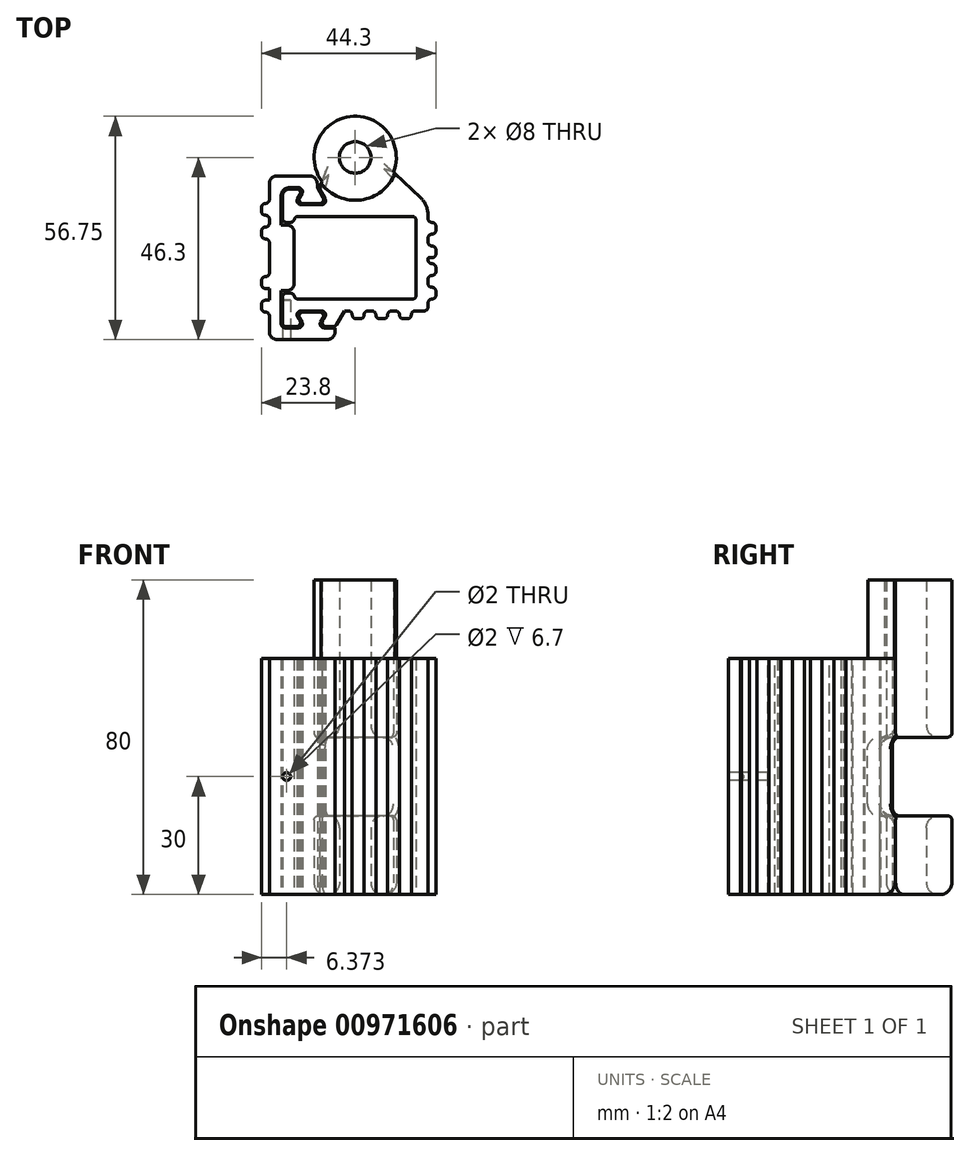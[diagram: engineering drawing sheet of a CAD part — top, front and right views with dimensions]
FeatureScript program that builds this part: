
annotation { "Feature Type Name" : "Feature", "Feature Type Description" : "" }
export const myFeature = defineFeature(function(context is Context, id is Id, definition is map)
    precondition{}
    {
        {
            var Q0;
            Q0=qCreatedBy(makeId("Top.planeOp"),FACE);
            var sketch = newSketch(context, id + "F0", { "sketchPlane" : qUnion([Q0])});
            skLineSegment(sketch, "E0.bottom", {"start": v(15.5, -10.5) * mm, "end": v(-15.5, -10.5) * mm, "construction": true});
            skLineSegment(sketch, "E0.top", {"start": v(15.5, 10.5) * mm, "end": v(-15.5, 10.5) * mm, "construction": true});
            skLineSegment(sketch, "E0.left", {"start": v(15.5, -10.5) * mm, "end": v(15.5, 10.5) * mm, "construction": true});
            skLineSegment(sketch, "E0.right", {"start": v(-15.5, -10.5) * mm, "end": v(-15.5, 10.25) * mm, "construction": true});
            skPoint(sketch, "E0.middle", {"position": v(0, 0) * mm});
            skLineSegment(sketch, "E1", {"start": v(-15.5, 0) * mm, "end": v(-15.5, -10.5) * mm});
            skLineSegment(sketch, "E2", {"start": v(15.5, -10.5) * mm, "end": v(15.5, 0) * mm});
            skLineSegment(sketch, "E3", {"start": v(15.5, 0) * mm, "end": v(18.5, 0) * mm});
            skLineSegment(sketch, "E4", {"start": v(-1.76, -13.5) * mm, "end": v(-2.76, -13.5) * mm});
            skLineSegment(sketch, "E5", {"start": v(-15.5, -10.5) * mm, "end": v(-15.5, -9) * mm});
            skLineSegment(sketch, "E6", {"start": v(-15.5, -9) * mm, "end": v(-17.5, -9) * mm});
            skLineSegment(sketch, "E7", {"start": v(-18.5, -10) * mm, "end": v(-18.5, -13.5) * mm});
            skLineSegment(sketch, "E8", {"start": v(-14.63, -15) * mm, "end": v(-14.06, -16) * mm});
            skLineSegment(sketch, "E9", {"start": v(-8.24, -16) * mm, "end": v(-7.67, -15) * mm});
            skLineSegment(sketch, "E10", {"start": v(-8.53, -13.5) * mm, "end": v(-13.77, -13.5) * mm});
            skLineSegment(sketch, "E11", {"start": v(-2.76, -13.5) * mm, "end": v(-5.07, -17.5) * mm});
            skLineSegment(sketch, "E12", {"start": v(-5.07, -17.5) * mm, "end": v(-7.38, -17.5) * mm});
            skLineSegment(sketch, "E13", {"start": v(-14.92, -17.5) * mm, "end": v(-17.5, -17.5) * mm});
            skLineSegment(sketch, "E14", {"start": v(-18.5, -16.5) * mm, "end": v(-18.5, -13.5) * mm});
            skLineSegment(sketch, "E15", {"start": v(-15.5, -13.5) * mm, "end": v(-15.5, -13.5) * mm});
            skLineSegment(sketch, "E16", {"start": v(-6.8, -13.5) * mm, "end": v(-15.5, -13.5) * mm});
            skLineSegment(sketch, "E17", {"start": v(-18.44, -13.5) * mm, "end": v(-18.5, -13.5) * mm});
            skLineSegment(sketch, "E18.0", {"start": v(-18.8, -9) * mm, "end": v(-18.8, -13.5) * mm});
            skLineSegment(sketch, "E18.1", {"start": v(-18.8, -16.8) * mm, "end": v(-18.8, -13.5) * mm});
            skLineSegment(sketch, "E18.2", {"start": v(-14.4, -17.8) * mm, "end": v(-17.8, -17.8) * mm});
            skLineSegment(sketch, "E18.3", {"start": v(-5.13, -17.8) * mm, "end": v(-7.9, -17.8) * mm});
            skLineSegment(sketch, "E18.4", {"start": v(-8.76, -16.3) * mm, "end": v(-8.19, -15.3) * mm});
            skLineSegment(sketch, "E18.5", {"start": v(-9.05, -13.8) * mm, "end": v(-13.25, -13.8) * mm});
            skLineSegment(sketch, "E18.6", {"start": v(-14.11, -15.3) * mm, "end": v(-13.54, -16.3) * mm});
            skLineSegment(sketch, "E19", {"start": v(-5.13, -17.8) * mm, "end": v(-5.13, -18.8) * mm});
            skLineSegment(sketch, "E20", {"start": v(-7.13, -20.8) * mm, "end": v(-19.8, -20.8) * mm});
            skLineSegment(sketch, "E21", {"start": v(-21.8, -18.8) * mm, "end": v(-21.8, -9) * mm});
            skLineSegment(sketch, "E22", {"start": v(-15.5, -10.5) * mm, "end": v(15.5, -10.5) * mm});
            skLineSegment(sketch, "E23.MirrorCS", {"start": v(-15.5, 9) * mm, "end": v(-18.5, 9) * mm});
            skLineSegment(sketch, "E24.MirrorCS", {"start": v(-18.44, 13.5) * mm, "end": v(-18.5, 13.5) * mm});
            skLineSegment(sketch, "E25.MirrorCS", {"start": v(-8.53, 13.5) * mm, "end": v(-13.77, 13.5) * mm});
            skLineSegment(sketch, "E26.MirrorCS", {"start": v(-14.63, 15) * mm, "end": v(-14.06, 16) * mm});
            skLineSegment(sketch, "E27.MirrorCS", {"start": v(-6.8, 13.5) * mm, "end": v(-15.5, 13.5) * mm});
            skLineSegment(sketch, "E28.MirrorCS", {"start": v(-9.1, 17.5) * mm, "end": v(-7.67, 15) * mm});
            skLineSegment(sketch, "E29.MirrorCS", {"start": v(-9.63, 17.8) * mm, "end": v(-8.19, 15.3) * mm});
            skLineSegment(sketch, "E30.MirrorCS", {"start": v(-15.5, 13.5) * mm, "end": v(-15.5, 13.5) * mm});
            skLineSegment(sketch, "E31.MirrorCS", {"start": v(-14.4, 17.8) * mm, "end": v(-16.8, 17.8) * mm});
            skLineSegment(sketch, "E32.MirrorCS", {"start": v(-9.05, 13.8) * mm, "end": v(-13.25, 13.8) * mm});
            skLineSegment(sketch, "E33.MirrorCS", {"start": v(-14.11, 15.3) * mm, "end": v(-13.54, 16.3) * mm});
            skLineSegment(sketch, "E34.MirrorCS", {"start": v(-14.92, 17.5) * mm, "end": v(-16.5, 17.5) * mm});
            skLineSegment(sketch, "E35.MirrorCS", {"start": v(-18.5, 15.5) * mm, "end": v(-18.5, 13.5) * mm});
            skLineSegment(sketch, "E36.MirrorCS", {"start": v(-18.8, 15.8) * mm, "end": v(-18.8, 13.5) * mm});
            skLineSegment(sketch, "E37.MirrorCS", {"start": v(-21.8, 18.8) * mm, "end": v(-21.8, 9) * mm});
            skLineSegment(sketch, "E38.MirrorCS", {"start": v(-15.5, 9) * mm, "end": v(-17.5, 9) * mm});
            skLineSegment(sketch, "E39.MirrorCS", {"start": v(-18.5, 10) * mm, "end": v(-18.5, 13.5) * mm});
            skLineSegment(sketch, "E40.MirrorCS", {"start": v(-18.8, 9) * mm, "end": v(-18.8, 13.5) * mm});
            skLineSegment(sketch, "E41.MirrorCS", {"start": v(-15.5, 6.37) * mm, "end": v(-15.5, -6.38) * mm, "construction": true});
            skLineSegment(sketch, "E42.MirrorCS", {"start": v(15.5, 10.5) * mm, "end": v(-15.25, 10.5) * mm, "construction": true});
            skLineSegment(sketch, "E43", {"start": v(-15.5, 10.5) * mm, "end": v(15.5, 10.5) * mm});
            skLineSegment(sketch, "E44", {"start": v(15.5, 0) * mm, "end": v(15.5, 10.5) * mm});
            skLineSegment(sketch, "E45", {"start": v(-15.5, 10.5) * mm, "end": v(-15.5, 9) * mm});
            skLineSegment(sketch, "E46", {"start": v(-21.8, -9) * mm, "end": v(-21.8, 9) * mm});
            skLineSegment(sketch, "E47", {"start": v(0, 10.5) * mm, "end": v(0, 25.5) * mm, "construction": true});
            skCircle(sketch, "E48", {"center": v(0, 25.5) * mm, "radius": 4 * mm});
            skLineSegment(sketch, "E49", {"start": v(-9.63, 17.8) * mm, "end": v(-9.63, 18.8) * mm});
            skLineSegment(sketch, "E50", {"start": v(-11.63, 20.8) * mm, "end": v(-19.8, 20.8) * mm});
            skArc(sketch, "E51", {"start": v(9.72, 21.68) * mm, "mid": v(-1.34, 35.86) * mm, "end": v(-8.44, 19.34) * mm});
            skLineSegment(sketch, "E52", {"start": v(-8.44, 19.34) * mm, "end": v(-9.1, 17.5) * mm});
            skLineSegment(sketch, "E53", {"start": v(9.72, 21.68) * mm, "end": v(18.5, 13.5) * mm});
            skLineSegment(sketch, "E54", {"start": v(19.5, -10.5) * mm, "end": v(19.5, -10.5) * mm});
            skLineSegment(sketch, "E55", {"start": v(20.5, -9.5) * mm, "end": v(20.5, -8.5) * mm});
            skLineSegment(sketch, "E56", {"start": v(19.5, -7.5) * mm, "end": v(19.5, -7.5) * mm});
            skLineSegment(sketch, "E57", {"start": v(18.5, -6.5) * mm, "end": v(18.5, -5.5) * mm});
            skLineSegment(sketch, "E58", {"start": v(19.5, -4.5) * mm, "end": v(19.5, -4.5) * mm});
            skLineSegment(sketch, "E59", {"start": v(20.5, -3.5) * mm, "end": v(20.5, -2.5) * mm});
            skLineSegment(sketch, "E60", {"start": v(19.5, -1.5) * mm, "end": v(19.5, -1.5) * mm});
            skLineSegment(sketch, "E61", {"start": v(18.5, -0.5) * mm, "end": v(18.5, -0.25) * mm});
            skLineSegment(sketch, "E62", {"start": v(20.5, 1) * mm, "end": v(20.5, 2) * mm});
            skLineSegment(sketch, "E63", {"start": v(19.5, 3) * mm, "end": v(19.5, 3) * mm});
            skLineSegment(sketch, "E64", {"start": v(18.5, 4) * mm, "end": v(18.5, 5) * mm});
            skLineSegment(sketch, "E65", {"start": v(19.5, 6) * mm, "end": v(19.5, 6) * mm});
            skLineSegment(sketch, "E66", {"start": v(20.5, 7) * mm, "end": v(20.5, 8) * mm});
            skLineSegment(sketch, "E67", {"start": v(19.5, 9) * mm, "end": v(19.5, 9) * mm});
            skLineSegment(sketch, "E68", {"start": v(18.5, 10) * mm, "end": v(18.5, 11.5) * mm});
            skLineSegment(sketch, "E69", {"start": v(19.5, 0) * mm, "end": v(18.75, 0) * mm});
            skLineSegment(sketch, "E70", {"start": v(18.5, 13.5) * mm, "end": v(18.5, 11.82) * mm});
            skLineSegment(sketch, "E71", {"start": v(18.5, -11.5) * mm, "end": v(18.5, -12.5) * mm});
            skLineSegment(sketch, "E72", {"start": v(18.5, 11.82) * mm, "end": v(18.5, 11.5) * mm});
            skLineSegment(sketch, "E73", {"start": v(-0.76, -14.5) * mm, "end": v(-0.76, -14.5) * mm});
            skLineSegment(sketch, "E74", {"start": v(0.24, -15.5) * mm, "end": v(1.24, -15.5) * mm});
            skLineSegment(sketch, "E75", {"start": v(2.24, -14.5) * mm, "end": v(2.24, -14.5) * mm});
            skLineSegment(sketch, "E76", {"start": v(3.24, -13.5) * mm, "end": v(4.24, -13.5) * mm});
            skLineSegment(sketch, "E77", {"start": v(5.24, -14.5) * mm, "end": v(5.24, -14.5) * mm});
            skLineSegment(sketch, "E78", {"start": v(6.24, -15.5) * mm, "end": v(7.24, -15.5) * mm});
            skLineSegment(sketch, "E79", {"start": v(8.24, -14.5) * mm, "end": v(8.24, -14.5) * mm});
            skLineSegment(sketch, "E80", {"start": v(9.24, -13.5) * mm, "end": v(10.24, -13.5) * mm});
            skLineSegment(sketch, "E81", {"start": v(11.24, -14.5) * mm, "end": v(11.24, -14.5) * mm});
            skLineSegment(sketch, "E82", {"start": v(12.24, -15.5) * mm, "end": v(13.24, -15.5) * mm});
            skLineSegment(sketch, "E83", {"start": v(14.24, -14.5) * mm, "end": v(14.24, -14.5) * mm});
            skPoint(sketch, "E84.visualSharp", {"position": v(-0.76, -15.5) * mm});
            skArc(sketch, "E84.filletArc", {"start": v(-0.76, -14.5) * mm, "mid": v(-0.47, -15.2) * mm, "end": v(0.24, -15.5) * mm});
            skPoint(sketch, "E85.newPointA", {"position": v(18.5, -13.5) * mm});
            skPoint(sketch, "E85.newPointB", {"position": v(-0.76, -13.5) * mm});
            skArc(sketch, "E85.filletArc", {"start": v(-0.76, -14.5) * mm, "mid": v(-1.05, -13.8) * mm, "end": v(-1.76, -13.5) * mm});
            skPoint(sketch, "E86.visualSharp", {"position": v(2.24, -15.5) * mm});
            skArc(sketch, "E86.filletArc", {"start": v(1.24, -15.5) * mm, "mid": v(1.95, -15.2) * mm, "end": v(2.24, -14.5) * mm});
            skPoint(sketch, "E87.visualSharp", {"position": v(2.24, -13.5) * mm});
            skArc(sketch, "E87.filletArc", {"start": v(3.24, -13.5) * mm, "mid": v(2.53, -13.8) * mm, "end": v(2.24, -14.5) * mm});
            skPoint(sketch, "E88.visualSharp", {"position": v(5.24, -13.5) * mm});
            skArc(sketch, "E88.filletArc", {"start": v(5.24, -14.5) * mm, "mid": v(4.95, -13.8) * mm, "end": v(4.24, -13.5) * mm});
            skPoint(sketch, "E89.visualSharp", {"position": v(5.24, -15.5) * mm});
            skArc(sketch, "E89.filletArc", {"start": v(5.24, -14.5) * mm, "mid": v(5.53, -15.2) * mm, "end": v(6.24, -15.5) * mm});
            skPoint(sketch, "E90.visualSharp", {"position": v(8.24, -15.5) * mm});
            skArc(sketch, "E90.filletArc", {"start": v(7.24, -15.5) * mm, "mid": v(7.95, -15.2) * mm, "end": v(8.24, -14.5) * mm});
            skPoint(sketch, "E91.visualSharp", {"position": v(8.24, -13.5) * mm});
            skArc(sketch, "E91.filletArc", {"start": v(9.24, -13.5) * mm, "mid": v(8.53, -13.8) * mm, "end": v(8.24, -14.5) * mm});
            skPoint(sketch, "E92.visualSharp", {"position": v(11.24, -13.5) * mm});
            skArc(sketch, "E92.filletArc", {"start": v(11.24, -14.5) * mm, "mid": v(10.95, -13.8) * mm, "end": v(10.24, -13.5) * mm});
            skPoint(sketch, "E93.visualSharp", {"position": v(11.24, -15.5) * mm});
            skArc(sketch, "E93.filletArc", {"start": v(11.24, -14.5) * mm, "mid": v(11.53, -15.2) * mm, "end": v(12.24, -15.5) * mm});
            skPoint(sketch, "E94.visualSharp", {"position": v(14.24, -15.5) * mm});
            skArc(sketch, "E94.filletArc", {"start": v(13.24, -15.5) * mm, "mid": v(13.95, -15.2) * mm, "end": v(14.24, -14.5) * mm});
            skLineSegment(sketch, "E95", {"start": v(15.24, -13.5) * mm, "end": v(17.5, -13.5) * mm});
            skPoint(sketch, "E96.visualSharp", {"position": v(14.24, -13.5) * mm});
            skArc(sketch, "E96.filletArc", {"start": v(15.24, -13.5) * mm, "mid": v(14.53, -13.8) * mm, "end": v(14.24, -14.5) * mm});
            skArc(sketch, "E97.filletArc", {"start": v(17.5, -13.5) * mm, "mid": v(18.2, -13.2) * mm, "end": v(18.5, -12.5) * mm});
            skPoint(sketch, "E98.visualSharp", {"position": v(18.5, -10.5) * mm});
            skArc(sketch, "E98.filletArc", {"start": v(19.5, -10.5) * mm, "mid": v(18.8, -10.8) * mm, "end": v(18.5, -11.5) * mm});
            skPoint(sketch, "E99.visualSharp", {"position": v(20.5, -10.5) * mm});
            skArc(sketch, "E99.filletArc", {"start": v(19.5, -10.5) * mm, "mid": v(20.2, -10.2) * mm, "end": v(20.5, -9.5) * mm});
            skPoint(sketch, "E100.visualSharp", {"position": v(20.5, -7.5) * mm});
            skArc(sketch, "E100.filletArc", {"start": v(20.5, -8.5) * mm, "mid": v(20.2, -7.8) * mm, "end": v(19.5, -7.5) * mm});
            skPoint(sketch, "E101.visualSharp", {"position": v(18.5, -7.5) * mm});
            skArc(sketch, "E101.filletArc", {"start": v(18.5, -6.5) * mm, "mid": v(18.8, -7.2) * mm, "end": v(19.5, -7.5) * mm});
            skPoint(sketch, "E102.visualSharp", {"position": v(18.5, -4.5) * mm});
            skArc(sketch, "E102.filletArc", {"start": v(19.5, -4.5) * mm, "mid": v(18.8, -4.8) * mm, "end": v(18.5, -5.5) * mm});
            skPoint(sketch, "E103.visualSharp", {"position": v(20.5, -4.5) * mm});
            skArc(sketch, "E103.filletArc", {"start": v(19.5, -4.5) * mm, "mid": v(20.2, -4.2) * mm, "end": v(20.5, -3.5) * mm});
            skPoint(sketch, "E104.visualSharp", {"position": v(20.5, -1.5) * mm});
            skArc(sketch, "E104.filletArc", {"start": v(20.5, -2.5) * mm, "mid": v(20.2, -1.8) * mm, "end": v(19.5, -1.5) * mm});
            skPoint(sketch, "E105.visualSharp", {"position": v(18.5, -1.5) * mm});
            skArc(sketch, "E105.filletArc", {"start": v(18.5, -0.5) * mm, "mid": v(18.8, -1.2) * mm, "end": v(19.5, -1.5) * mm});
            skPoint(sketch, "E106.visualSharp", {"position": v(18.5, 0) * mm});
            skArc(sketch, "E106.filletArc", {"start": v(18.75, 0) * mm, "mid": v(18.57, -0.07) * mm, "end": v(18.5, -0.25) * mm});
            skPoint(sketch, "E107.visualSharp", {"position": v(20.5, 0) * mm});
            skArc(sketch, "E107.filletArc", {"start": v(19.5, 0) * mm, "mid": v(20.2, 0.3) * mm, "end": v(20.5, 1) * mm});
            skPoint(sketch, "E108.visualSharp", {"position": v(20.5, 3) * mm});
            skArc(sketch, "E108.filletArc", {"start": v(20.5, 2) * mm, "mid": v(20.2, 2.7) * mm, "end": v(19.5, 3) * mm});
            skPoint(sketch, "E109.visualSharp", {"position": v(18.5, 3) * mm});
            skArc(sketch, "E109.filletArc", {"start": v(18.5, 4) * mm, "mid": v(18.8, 3.3) * mm, "end": v(19.5, 3) * mm});
            skPoint(sketch, "E110.visualSharp", {"position": v(18.5, 6) * mm});
            skArc(sketch, "E110.filletArc", {"start": v(19.5, 6) * mm, "mid": v(18.8, 5.7) * mm, "end": v(18.5, 5) * mm});
            skPoint(sketch, "E111.visualSharp", {"position": v(20.5, 6) * mm});
            skArc(sketch, "E111.filletArc", {"start": v(19.5, 6) * mm, "mid": v(20.2, 6.3) * mm, "end": v(20.5, 7) * mm});
            skPoint(sketch, "E112.visualSharp", {"position": v(20.5, 9) * mm});
            skArc(sketch, "E112.filletArc", {"start": v(20.5, 8) * mm, "mid": v(20.2, 8.7) * mm, "end": v(19.5, 9) * mm});
            skPoint(sketch, "E113.visualSharp", {"position": v(18.5, 9) * mm});
            skArc(sketch, "E113.filletArc", {"start": v(18.5, 10) * mm, "mid": v(18.8, 9.3) * mm, "end": v(19.5, 9) * mm});
            skPoint(sketch, "E114.visualSharp", {"position": v(-15.5, 10.5) * mm});
            skArc(sketch, "E114.filletArc", {"start": v(-15.25, 10.5) * mm, "mid": v(-15.43, 10.43) * mm, "end": v(-15.5, 10.25) * mm, "construction": true});
            skPoint(sketch, "E115.visualSharp", {"position": v(-5.13, -20.8) * mm});
            skArc(sketch, "E115.filletArc", {"start": v(-7.13, -20.8) * mm, "mid": v(-5.71, -20.21) * mm, "end": v(-5.13, -18.8) * mm});
            skPoint(sketch, "E116.visualSharp", {"position": v(-9.63, 20.8) * mm});
            skArc(sketch, "E116.filletArc", {"start": v(-9.63, 18.8) * mm, "mid": v(-10.21, 20.21) * mm, "end": v(-11.63, 20.8) * mm});
            skPoint(sketch, "E117.visualSharp", {"position": v(-21.8, 20.8) * mm});
            skArc(sketch, "E117.filletArc", {"start": v(-19.8, 20.8) * mm, "mid": v(-21.21, 20.21) * mm, "end": v(-21.8, 18.8) * mm});
            skPoint(sketch, "E118.visualSharp", {"position": v(-18.5, 17.5) * mm});
            skArc(sketch, "E118.filletArc", {"start": v(-16.5, 17.5) * mm, "mid": v(-17.91, 16.91) * mm, "end": v(-18.5, 15.5) * mm});
            skPoint(sketch, "E119.visualSharp", {"position": v(-18.8, 17.8) * mm});
            skArc(sketch, "E119.filletArc", {"start": v(-16.8, 17.8) * mm, "mid": v(-18.21, 17.21) * mm, "end": v(-18.8, 15.8) * mm});
            skPoint(sketch, "E120.visualSharp", {"position": v(-14.98, 13.8) * mm});
            skArc(sketch, "E120.filletArc", {"start": v(-14.11, 15.3) * mm, "mid": v(-14.11, 14.3) * mm, "end": v(-13.25, 13.8) * mm});
            skPoint(sketch, "E121.visualSharp", {"position": v(-15.5, 13.5) * mm});
            skArc(sketch, "E121.filletArc", {"start": v(-14.63, 15) * mm, "mid": v(-14.63, 14) * mm, "end": v(-13.77, 13.5) * mm});
            skPoint(sketch, "E122.visualSharp", {"position": v(-13.2, 17.5) * mm});
            skArc(sketch, "E122.filletArc", {"start": v(-14.06, 16) * mm, "mid": v(-14.06, 17) * mm, "end": v(-14.92, 17.5) * mm});
            skPoint(sketch, "E123.visualSharp", {"position": v(-12.67, 17.8) * mm});
            skArc(sketch, "E123.filletArc", {"start": v(-13.54, 16.3) * mm, "mid": v(-13.54, 17.3) * mm, "end": v(-14.4, 17.8) * mm});
            skPoint(sketch, "E124.visualSharp", {"position": v(-7.32, 13.8) * mm});
            skArc(sketch, "E124.filletArc", {"start": v(-9.05, 13.8) * mm, "mid": v(-8.19, 14.3) * mm, "end": v(-8.19, 15.3) * mm});
            skPoint(sketch, "E125.visualSharp", {"position": v(-6.8, 13.5) * mm});
            skArc(sketch, "E125.filletArc", {"start": v(-8.53, 13.5) * mm, "mid": v(-7.67, 14) * mm, "end": v(-7.67, 15) * mm});
            skPoint(sketch, "E126.visualSharp", {"position": v(-18.5, -17.5) * mm});
            skArc(sketch, "E126.filletArc", {"start": v(-18.5, -16.5) * mm, "mid": v(-18.2, -17.2) * mm, "end": v(-17.5, -17.5) * mm});
            skPoint(sketch, "E127.visualSharp", {"position": v(-18.8, -17.8) * mm});
            skArc(sketch, "E127.filletArc", {"start": v(-18.8, -16.8) * mm, "mid": v(-18.5, -17.5) * mm, "end": v(-17.8, -17.8) * mm});
            skPoint(sketch, "E128.visualSharp", {"position": v(-12.67, -17.8) * mm});
            skArc(sketch, "E128.filletArc", {"start": v(-14.4, -17.8) * mm, "mid": v(-13.54, -17.3) * mm, "end": v(-13.54, -16.3) * mm});
            skPoint(sketch, "E129.visualSharp", {"position": v(-13.2, -17.5) * mm});
            skArc(sketch, "E129.filletArc", {"start": v(-14.92, -17.5) * mm, "mid": v(-14.06, -17) * mm, "end": v(-14.06, -16) * mm});
            skPoint(sketch, "E130.visualSharp", {"position": v(-15.5, -13.5) * mm});
            skArc(sketch, "E130.filletArc", {"start": v(-13.77, -13.5) * mm, "mid": v(-14.63, -14) * mm, "end": v(-14.63, -15) * mm});
            skPoint(sketch, "E131.visualSharp", {"position": v(-14.98, -13.8) * mm});
            skArc(sketch, "E131.filletArc", {"start": v(-13.25, -13.8) * mm, "mid": v(-14.11, -14.3) * mm, "end": v(-14.11, -15.3) * mm});
            skPoint(sketch, "E132.visualSharp", {"position": v(-7.32, -13.8) * mm});
            skArc(sketch, "E132.filletArc", {"start": v(-8.19, -15.3) * mm, "mid": v(-8.19, -14.3) * mm, "end": v(-9.05, -13.8) * mm});
            skPoint(sketch, "E133.visualSharp", {"position": v(-6.8, -13.5) * mm});
            skArc(sketch, "E133.filletArc", {"start": v(-7.67, -15) * mm, "mid": v(-7.67, -14) * mm, "end": v(-8.53, -13.5) * mm});
            skPoint(sketch, "E134.visualSharp", {"position": v(-9.1, -17.5) * mm});
            skArc(sketch, "E134.filletArc", {"start": v(-8.24, -16) * mm, "mid": v(-8.24, -17) * mm, "end": v(-7.38, -17.5) * mm});
            skPoint(sketch, "E135.visualSharp", {"position": v(-9.63, -17.8) * mm});
            skArc(sketch, "E135.filletArc", {"start": v(-8.76, -16.3) * mm, "mid": v(-8.76, -17.3) * mm, "end": v(-7.9, -17.8) * mm});
            skLineSegment(sketch, "E136", {"start": v(-15.5, 8.37) * mm, "end": v(-15.5, -8.38) * mm});
            skLineSegment(sketch, "E137", {"start": v(-17.5, -8.38) * mm, "end": v(-18.8, -8.38) * mm});
            skLineSegment(sketch, "E138", {"start": v(-17.5, 8.37) * mm, "end": v(-18.8, 8.37) * mm});
            skLineSegment(sketch, "E139", {"start": v(-18.8, -8.38) * mm, "end": v(-18.8, -9) * mm});
            skLineSegment(sketch, "E140", {"start": v(-18.8, 8.37) * mm, "end": v(-18.8, 9) * mm});
            skPoint(sketch, "E141.visualSharp", {"position": v(-21.8, -20.8) * mm});
            skArc(sketch, "E141.filletArc", {"start": v(-21.8, -18.8) * mm, "mid": v(-21.21, -20.21) * mm, "end": v(-19.8, -20.8) * mm});
            skArc(sketch, "E142.filletArc", {"start": v(-15.5, 6.37) * mm, "mid": v(-16.09, 7.78) * mm, "end": v(-17.5, 8.37) * mm});
            skPoint(sketch, "E143.newPointB", {"position": v(-15.5, -10.5) * mm});
            skArc(sketch, "E143.filletArc", {"start": v(-17.5, -8.38) * mm, "mid": v(-16.09, -7.8) * mm, "end": v(-15.5, -6.38) * mm});
            skPoint(sketch, "E144.visualSharp", {"position": v(-18.5, 9) * mm});
            skArc(sketch, "E144.filletArc", {"start": v(-18.5, 10) * mm, "mid": v(-18.2, 9.3) * mm, "end": v(-17.5, 9) * mm});
            skPoint(sketch, "E145.visualSharp", {"position": v(-18.5, -9) * mm});
            skArc(sketch, "E145.filletArc", {"start": v(-17.5, -9) * mm, "mid": v(-18.2, -9.3) * mm, "end": v(-18.5, -10) * mm});
            skSolve(sketch);
        }
        {
            var Q0;
            Q0=makeQuery(id+"F0.imprint","IMPRINT",FACE,{"disambiguationData":[TD([[makeQuery(id+"F0.imprint","IMPRINT",EDGE,{"derivedFrom":sQuery(id+"F0.wireOp",EDGE,"E2")}),-1.0]])]});
            var Q1;
            Q1=makeQuery(id+"F0.imprint","IMPRINT",FACE,{"disambiguationData":[TD([[makeQuery(id+"F0.imprint","IMPRINT",EDGE,{"derivedFrom":sQuery(id+"F0.wireOp",EDGE,"E18.0")}),-1.0]])]});
            extrude(context, id + "F1", {"entities" : qUnion([Q0, Q1]), "depth" : 60 * mm, "offsetDistance" : 25 * mm});
        }
        {
            var Q0;
            Q0=makeQuery(id+"F1.opExtrude","SWEPT_EDGE",EDGE,{"disambiguationData":[OSD([sQuery(id+"F0.wireOp",EDGE,"E43"),sQuery(id+"F0.wireOp",EDGE,"E44")])]});
            var Q1;
            Q1=makeQuery(id+"F1.opExtrude","SWEPT_EDGE",EDGE,{"disambiguationData":[OSD([sQuery(id+"F0.wireOp",EDGE,"E2"),sQuery(id+"F0.wireOp",EDGE,"E22")])]});
            var Q2;
            Q2=makeQuery(id+"F1.opExtrude","SWEPT_EDGE",EDGE,{"disambiguationData":[OSD([sQuery(id+"F0.wireOp",EDGE,"E5"),sQuery(id+"F0.wireOp",EDGE,"E22")])]});
            var Q3;
            Q3=makeQuery(id+"F1.opExtrude","SWEPT_EDGE",EDGE,{"disambiguationData":[OSD([sQuery(id+"F0.wireOp",EDGE,"E43"),sQuery(id+"F0.wireOp",EDGE,"E45")])]});
            fillet(context, id + "F2", {"entities" : qUnion([Q0, Q1, Q2, Q3]), "radius" : 1 * mm, "tangentPropagation" : true, "allowEdgeOverflow" : false});
        }
        {
            var Q0;
            Q0=makeQuery(id+"F1.opExtrude","SWEPT_EDGE",EDGE,{"disambiguationData":[OSD([sQuery(id+"F0.wireOp",EDGE,"E38.MirrorCS"),sQuery(id+"F0.wireOp",EDGE,"E45")])]});
            var Q1;
            {var subQ0=sQuery(id+"F0.wireOp",EDGE,"E5");Q1=makeQuery(id+"F2.opFillet","BLEND_EDGE",EDGE,{"blendedFrom":[makeQuery(id+"F1.opExtrude","SWEPT_EDGE",EDGE,{"disambiguationData":[OSD([subQ0,sQuery(id+"F0.wireOp",EDGE,"E22")])]}),makeQuery(id+"F1.opExtrude","SWEPT_FACE",FACE,{"disambiguationData":[OSD([subQ0])]})],"blendedInto":[makeQuery(id+"F1.opExtrude","SWEPT_FACE",FACE,{"disambiguationData":[OSD([subQ0])]})]});}
            var Q2;
            Q2=makeQuery(id+"F1.opExtrude","SWEPT_EDGE",EDGE,{"disambiguationData":[OSD([sQuery(id+"F0.wireOp",EDGE,"E5"),sQuery(id+"F0.wireOp",EDGE,"E6")])]});
            var Q3;
            Q3=makeQuery(id+"F1.opExtrude","SWEPT_EDGE",EDGE,{"disambiguationData":[OSD([sQuery(id+"F0.wireOp",EDGE,"E11"),sQuery(id+"F0.wireOp",EDGE,"E12")])]});
            fillet(context, id + "F3", {"entities" : qUnion([Q0, Q1, Q2, Q3]), "radius" : 1 * mm, "tangentPropagation" : true, "allowEdgeOverflow" : false});
        }
        {
            var Q0;
            Q0=makeQuery(id+"F1.opExtrude","SWEPT_EDGE",EDGE,{"disambiguationData":[OSD([sQuery(id+"F0.wireOp",EDGE,"E53"),sQuery(id+"F0.wireOp",EDGE,"E70")])]});
            fillet(context, id + "F4", {"entities" : qUnion([Q0]), "radius" : 6 * mm, "tangentPropagation" : true, "allowEdgeOverflow" : false});
        }
        {
            var Q0;
            Q0=makeQuery(id+"F1.opExtrude","SWEPT_FACE",FACE,{"disambiguationData":[OSD([sQuery(id+"F0.wireOp",EDGE,"E21"),sQuery(id+"F0.wireOp",EDGE,"E37.MirrorCS"),sQuery(id+"F0.wireOp",EDGE,"E46")])]});
            var sketch = newSketch(context, id + "F5", { "sketchPlane" : qUnion([Q0])});
            skLineSegment(sketch, "E146", {"start": v(13.8, 60) * mm, "end": v(13.8, 0) * mm});
            skLineSegment(sketch, "E147", {"start": v(13.8, 0) * mm, "end": v(10.8, 0) * mm});
            skLineSegment(sketch, "E148", {"start": v(10.8, 0) * mm, "end": v(10.8, 60) * mm});
            skLineSegment(sketch, "E149", {"start": v(10.8, 60) * mm, "end": v(7.8, 60) * mm});
            skLineSegment(sketch, "E150", {"start": v(7.8, 60) * mm, "end": v(7.8, 0) * mm});
            skLineSegment(sketch, "E151", {"start": v(7.8, 0) * mm, "end": v(0, 0) * mm});
            skLineSegment(sketch, "E152", {"start": v(0, 60) * mm, "end": v(0, 0) * mm});
            skLineSegment(sketch, "E153", {"start": v(-4.8, 0) * mm, "end": v(-4.8, 60) * mm});
            skLineSegment(sketch, "E154", {"start": v(-4.8, 60) * mm, "end": v(-7.8, 60) * mm});
            skLineSegment(sketch, "E155", {"start": v(-7.8, 60) * mm, "end": v(-7.8, 0) * mm});
            skLineSegment(sketch, "E156", {"start": v(-7.8, 0) * mm, "end": v(-10.8, 0) * mm});
            skLineSegment(sketch, "E157", {"start": v(-10.8, 0) * mm, "end": v(-10.8, 60) * mm});
            skLineSegment(sketch, "E158", {"start": v(-10.8, 60) * mm, "end": v(-13.8, 60) * mm});
            skLineSegment(sketch, "E159", {"start": v(-13.8, 60) * mm, "end": v(-13.8, 0) * mm});
            skLineSegment(sketch, "E160", {"start": v(4.8, 60) * mm, "end": v(4.8, 0) * mm});
            skSolve(sketch);
        }
        {
            var Q0;
            {var subQ0=sQuery(id+"F5.wireOp",EDGE,"E157");Q0=makeQuery(id+"F5.imprint","IMPRINT",FACE,{"disambiguationData":[TD([[makeQuery(id+"F5.imprint","IMPRINT",EDGE,{"derivedFrom":subQ0}),1.0]])]});}
            var Q1;
            {var subQ0=sQuery(id+"F5.wireOp",EDGE,"E153");Q1=makeQuery(id+"F5.imprint","IMPRINT",FACE,{"disambiguationData":[TD([[makeQuery(id+"F5.imprint","IMPRINT",EDGE,{"derivedFrom":subQ0}),1.0]])]});}
            var Q2;
            {var subQ0=sQuery(id+"F5.wireOp",EDGE,"E150");Q2=makeQuery(id+"F5.imprint","IMPRINT",FACE,{"disambiguationData":[TD([[makeQuery(id+"F5.imprint","IMPRINT",EDGE,{"derivedFrom":subQ0}),-1.0]])]});}
            var Q3;
            {var subQ0=sQuery(id+"F5.wireOp",EDGE,"E146");Q3=makeQuery(id+"F5.imprint","IMPRINT",FACE,{"disambiguationData":[TD([[makeQuery(id+"F5.imprint","IMPRINT",EDGE,{"derivedFrom":subQ0}),-1.0]])]});}
            extrude(context, id + "F6", {"entities" : qUnion([Q0, Q1, Q2, Q3]), "operationType" : NewBodyOperationType.ADD, "depth" : 2 * mm, "offsetDistance" : 25 * mm});
        }
        {
            var Q0;
            Q0=makeQuery(id+"F6.opExtrude","CAP_EDGE",EDGE,{"disambiguationData":[OSD([sQuery(id+"F5.wireOp",EDGE,"E159")])],"isStart":false});
            var Q1;
            Q1=makeQuery(id+"F6.opExtrude","CAP_EDGE",EDGE,{"disambiguationData":[OSD([sQuery(id+"F5.wireOp",EDGE,"E157")])],"isStart":false});
            var Q2;
            Q2=makeQuery(id+"F6.opExtrude","CAP_EDGE",EDGE,{"disambiguationData":[OSD([sQuery(id+"F5.wireOp",EDGE,"E159")])],"isStart":true});
            var Q3;
            Q3=makeQuery(id+"F6.opExtrude","CAP_EDGE",EDGE,{"disambiguationData":[OSD([sQuery(id+"F5.wireOp",EDGE,"E155")])],"isStart":false});
            var Q4;
            Q4=makeQuery(id+"F6.opExtrude","CAP_EDGE",EDGE,{"disambiguationData":[OSD([sQuery(id+"F5.wireOp",EDGE,"E155")])],"isStart":true});
            var Q5;
            Q5=makeQuery(id+"F6.opExtrude","CAP_EDGE",EDGE,{"disambiguationData":[OSD([sQuery(id+"F5.wireOp",EDGE,"E153")])],"isStart":false});
            var Q6;
            Q6=makeQuery(id+"F6.opExtrude","CAP_EDGE",EDGE,{"disambiguationData":[OSD([sQuery(id+"F5.wireOp",EDGE,"E160")])],"isStart":true});
            var Q7;
            Q7=makeQuery(id+"F6.opExtrude","CAP_EDGE",EDGE,{"disambiguationData":[OSD([sQuery(id+"F5.wireOp",EDGE,"E160")])],"isStart":false});
            var Q8;
            Q8=makeQuery(id+"F6.opExtrude","CAP_EDGE",EDGE,{"disambiguationData":[OSD([sQuery(id+"F5.wireOp",EDGE,"E150")])],"isStart":false});
            var Q9;
            Q9=makeQuery(id+"F6.opExtrude","CAP_EDGE",EDGE,{"disambiguationData":[OSD([sQuery(id+"F5.wireOp",EDGE,"E148")])],"isStart":false});
            var Q10;
            Q10=makeQuery(id+"F6.opExtrude","CAP_EDGE",EDGE,{"disambiguationData":[OSD([sQuery(id+"F5.wireOp",EDGE,"E146")])],"isStart":false});
            var Q11;
            Q11=makeQuery(id+"F6.opExtrude","CAP_EDGE",EDGE,{"disambiguationData":[OSD([sQuery(id+"F5.wireOp",EDGE,"E148")])],"isStart":true});
            var Q12;
            Q12=makeQuery(id+"F6.opExtrude","CAP_EDGE",EDGE,{"disambiguationData":[OSD([sQuery(id+"F5.wireOp",EDGE,"E146")])],"isStart":true});
            var Q13;
            Q13=makeQuery(id+"F6.opExtrude","CAP_EDGE",EDGE,{"disambiguationData":[OSD([sQuery(id+"F5.wireOp",EDGE,"E150")])],"isStart":true});
            var Q14;
            Q14=makeQuery(id+"F6.opExtrude","CAP_EDGE",EDGE,{"disambiguationData":[OSD([sQuery(id+"F5.wireOp",EDGE,"E153")])],"isStart":true});
            var Q15;
            Q15=makeQuery(id+"F6.opExtrude","CAP_EDGE",EDGE,{"disambiguationData":[OSD([sQuery(id+"F5.wireOp",EDGE,"E157")])],"isStart":true});
            fillet(context, id + "F7", {"entities" : qUnion([Q0, Q1, Q2, Q3, Q4, Q5, Q6, Q7, Q8, Q9, Q10, Q11, Q12, Q13, Q14, Q15]), "radius" : 1 * mm, "tangentPropagation" : true, "allowEdgeOverflow" : false});
        }
        {
            var Q0;
            Q0=makeQuery(id+"F1.opExtrude","SWEPT_FACE",FACE,{"disambiguationData":[OSD([sQuery(id+"F0.wireOp",EDGE,"E20")])]});
            var sketch = newSketch(context, id + "F8", { "sketchPlane" : qUnion([Q0])});
            skCircle(sketch, "E161", {"center": v(-17.43, 30) * mm, "radius": 1 * mm});
            skPoint(sketch, "E161.centerSnap0", {"position": v(-19.8, 30) * mm});
            skSolve(sketch);
        }
        {
            var Q0;
            Q0=makeQuery(id+"F8.imprint","IMPRINT",FACE,{"disambiguationData":[TD([[makeQuery(id+"F8.imprint","IMPRINT",EDGE,{"derivedFrom":sQuery(id+"F8.wireOp",EDGE,"E161")}),1.0]])]});
            extrude(context, id + "F9", {"entities" : qUnion([Q0]), "operationType" : NewBodyOperationType.REMOVE, "oppositeDirection" : true, "depth" : 10 * mm, "offsetDistance" : 25 * mm});
        }
        {
            var Q0;
            Q0=makeQuery(id+"F1.opExtrude","CAP_FACE",FACE,{"disambiguationData":[OSD([sQuery(id+"F0.wireOp",EDGE,"E2"),sQuery(id+"F0.wireOp",EDGE,"E4"),sQuery(id+"F0.wireOp",EDGE,"E5"),sQuery(id+"F0.wireOp",EDGE,"E6"),sQuery(id+"F0.wireOp",EDGE,"E7"),sQuery(id+"F0.wireOp",EDGE,"E8"),sQuery(id+"F0.wireOp",EDGE,"E9"),sQuery(id+"F0.wireOp",EDGE,"E11"),sQuery(id+"F0.wireOp",EDGE,"E12"),sQuery(id+"F0.wireOp",EDGE,"E13"),sQuery(id+"F0.wireOp",EDGE,"E14"),sQuery(id+"F0.wireOp",EDGE,"E16"),sQuery(id+"F0.wireOp",EDGE,"E22"),sQuery(id+"F0.wireOp",EDGE,"E26.MirrorCS"),sQuery(id+"F0.wireOp",EDGE,"E27.MirrorCS"),sQuery(id+"F0.wireOp",EDGE,"E28.MirrorCS"),sQuery(id+"F0.wireOp",EDGE,"E34.MirrorCS"),sQuery(id+"F0.wireOp",EDGE,"E35.MirrorCS"),sQuery(id+"F0.wireOp",EDGE,"E38.MirrorCS"),sQuery(id+"F0.wireOp",EDGE,"E39.MirrorCS"),sQuery(id+"F0.wireOp",EDGE,"E43"),sQuery(id+"F0.wireOp",EDGE,"E44"),sQuery(id+"F0.wireOp",EDGE,"E45"),sQuery(id+"F0.wireOp",EDGE,"E48"),sQuery(id+"F0.wireOp",EDGE,"E51"),sQuery(id+"F0.wireOp",EDGE,"E52"),sQuery(id+"F0.wireOp",EDGE,"E53"),sQuery(id+"F0.wireOp",EDGE,"E55"),sQuery(id+"F0.wireOp",EDGE,"E57"),sQuery(id+"F0.wireOp",EDGE,"E59"),sQuery(id+"F0.wireOp",EDGE,"E61"),sQuery(id+"F0.wireOp",EDGE,"E62"),sQuery(id+"F0.wireOp",EDGE,"E64"),sQuery(id+"F0.wireOp",EDGE,"E66"),sQuery(id+"F0.wireOp",EDGE,"E68"),sQuery(id+"F0.wireOp",EDGE,"E69"),sQuery(id+"F0.wireOp",EDGE,"E70"),sQuery(id+"F0.wireOp",EDGE,"E71"),sQuery(id+"F0.wireOp",EDGE,"E72"),sQuery(id+"F0.wireOp",EDGE,"E74"),sQuery(id+"F0.wireOp",EDGE,"E76"),sQuery(id+"F0.wireOp",EDGE,"E78"),sQuery(id+"F0.wireOp",EDGE,"E80"),sQuery(id+"F0.wireOp",EDGE,"E82"),sQuery(id+"F0.wireOp",EDGE,"E84.filletArc"),sQuery(id+"F0.wireOp",EDGE,"E85.filletArc"),sQuery(id+"F0.wireOp",EDGE,"E86.filletArc"),sQuery(id+"F0.wireOp",EDGE,"E87.filletArc"),sQuery(id+"F0.wireOp",EDGE,"E88.filletArc"),sQuery(id+"F0.wireOp",EDGE,"E89.filletArc"),sQuery(id+"F0.wireOp",EDGE,"E90.filletArc"),sQuery(id+"F0.wireOp",EDGE,"E91.filletArc"),sQuery(id+"F0.wireOp",EDGE,"E92.filletArc"),sQuery(id+"F0.wireOp",EDGE,"E93.filletArc"),sQuery(id+"F0.wireOp",EDGE,"E94.filletArc"),sQuery(id+"F0.wireOp",EDGE,"E95"),sQuery(id+"F0.wireOp",EDGE,"E96.filletArc"),sQuery(id+"F0.wireOp",EDGE,"E97.filletArc"),sQuery(id+"F0.wireOp",EDGE,"E98.filletArc"),sQuery(id+"F0.wireOp",EDGE,"E99.filletArc"),sQuery(id+"F0.wireOp",EDGE,"E100.filletArc"),sQuery(id+"F0.wireOp",EDGE,"E101.filletArc"),sQuery(id+"F0.wireOp",EDGE,"E102.filletArc"),sQuery(id+"F0.wireOp",EDGE,"E103.filletArc"),sQuery(id+"F0.wireOp",EDGE,"E104.filletArc"),sQuery(id+"F0.wireOp",EDGE,"E105.filletArc"),sQuery(id+"F0.wireOp",EDGE,"E106.filletArc"),sQuery(id+"F0.wireOp",EDGE,"E107.filletArc"),sQuery(id+"F0.wireOp",EDGE,"E108.filletArc"),sQuery(id+"F0.wireOp",EDGE,"E109.filletArc"),sQuery(id+"F0.wireOp",EDGE,"E110.filletArc"),sQuery(id+"F0.wireOp",EDGE,"E111.filletArc"),sQuery(id+"F0.wireOp",EDGE,"E112.filletArc"),sQuery(id+"F0.wireOp",EDGE,"E113.filletArc"),sQuery(id+"F0.wireOp",EDGE,"E118.filletArc"),sQuery(id+"F0.wireOp",EDGE,"E121.filletArc"),sQuery(id+"F0.wireOp",EDGE,"E122.filletArc"),sQuery(id+"F0.wireOp",EDGE,"E125.filletArc"),sQuery(id+"F0.wireOp",EDGE,"E126.filletArc"),sQuery(id+"F0.wireOp",EDGE,"E129.filletArc"),sQuery(id+"F0.wireOp",EDGE,"E130.filletArc"),sQuery(id+"F0.wireOp",EDGE,"E133.filletArc"),sQuery(id+"F0.wireOp",EDGE,"E134.filletArc"),sQuery(id+"F0.wireOp",EDGE,"E144.filletArc"),sQuery(id+"F0.wireOp",EDGE,"E145.filletArc")])],"isStart":false});
            var sketch = newSketch(context, id + "F10", { "sketchPlane" : qUnion([Q0])});
            skCircle(sketch, "E162.0", {"center": v(0, 25.5) * mm, "radius": 10.89 * mm});
            skSolve(sketch);
        }
        {
            var Q0;
            Q0=makeQuery(id+"F10.imprint","IMPRINT",FACE,{"disambiguationData":[TD([[makeQuery(id+"F10.imprint","IMPRINT",EDGE,{"derivedFrom":makeQuery(id+"F1.opExtrude","CAP_EDGE",EDGE,{"disambiguationData":[OSD([sQuery(id+"F0.wireOp",EDGE,"E48")])],"isStart":false})}),-1.0]])]});
            extrude(context, id + "F11", {"entities" : qUnion([Q0]), "operationType" : NewBodyOperationType.ADD, "depth" : 20 * mm, "offsetDistance" : 25 * mm});
        }
        {
            var Q0;
            Q0=makeQuery(id+"F1.opExtrude","CAP_FACE",FACE,{"disambiguationData":[OSD([sQuery(id+"F0.wireOp",EDGE,"E2"),sQuery(id+"F0.wireOp",EDGE,"E4"),sQuery(id+"F0.wireOp",EDGE,"E5"),sQuery(id+"F0.wireOp",EDGE,"E6"),sQuery(id+"F0.wireOp",EDGE,"E7"),sQuery(id+"F0.wireOp",EDGE,"E8"),sQuery(id+"F0.wireOp",EDGE,"E9"),sQuery(id+"F0.wireOp",EDGE,"E11"),sQuery(id+"F0.wireOp",EDGE,"E12"),sQuery(id+"F0.wireOp",EDGE,"E13"),sQuery(id+"F0.wireOp",EDGE,"E14"),sQuery(id+"F0.wireOp",EDGE,"E16"),sQuery(id+"F0.wireOp",EDGE,"E22"),sQuery(id+"F0.wireOp",EDGE,"E26.MirrorCS"),sQuery(id+"F0.wireOp",EDGE,"E27.MirrorCS"),sQuery(id+"F0.wireOp",EDGE,"E28.MirrorCS"),sQuery(id+"F0.wireOp",EDGE,"E34.MirrorCS"),sQuery(id+"F0.wireOp",EDGE,"E35.MirrorCS"),sQuery(id+"F0.wireOp",EDGE,"E38.MirrorCS"),sQuery(id+"F0.wireOp",EDGE,"E39.MirrorCS"),sQuery(id+"F0.wireOp",EDGE,"E43"),sQuery(id+"F0.wireOp",EDGE,"E44"),sQuery(id+"F0.wireOp",EDGE,"E45"),sQuery(id+"F0.wireOp",EDGE,"E48"),sQuery(id+"F0.wireOp",EDGE,"E51"),sQuery(id+"F0.wireOp",EDGE,"E52"),sQuery(id+"F0.wireOp",EDGE,"E53"),sQuery(id+"F0.wireOp",EDGE,"E55"),sQuery(id+"F0.wireOp",EDGE,"E57"),sQuery(id+"F0.wireOp",EDGE,"E59"),sQuery(id+"F0.wireOp",EDGE,"E61"),sQuery(id+"F0.wireOp",EDGE,"E62"),sQuery(id+"F0.wireOp",EDGE,"E64"),sQuery(id+"F0.wireOp",EDGE,"E66"),sQuery(id+"F0.wireOp",EDGE,"E68"),sQuery(id+"F0.wireOp",EDGE,"E69"),sQuery(id+"F0.wireOp",EDGE,"E70"),sQuery(id+"F0.wireOp",EDGE,"E71"),sQuery(id+"F0.wireOp",EDGE,"E72"),sQuery(id+"F0.wireOp",EDGE,"E74"),sQuery(id+"F0.wireOp",EDGE,"E76"),sQuery(id+"F0.wireOp",EDGE,"E78"),sQuery(id+"F0.wireOp",EDGE,"E80"),sQuery(id+"F0.wireOp",EDGE,"E82"),sQuery(id+"F0.wireOp",EDGE,"E84.filletArc"),sQuery(id+"F0.wireOp",EDGE,"E85.filletArc"),sQuery(id+"F0.wireOp",EDGE,"E86.filletArc"),sQuery(id+"F0.wireOp",EDGE,"E87.filletArc"),sQuery(id+"F0.wireOp",EDGE,"E88.filletArc"),sQuery(id+"F0.wireOp",EDGE,"E89.filletArc"),sQuery(id+"F0.wireOp",EDGE,"E90.filletArc"),sQuery(id+"F0.wireOp",EDGE,"E91.filletArc"),sQuery(id+"F0.wireOp",EDGE,"E92.filletArc"),sQuery(id+"F0.wireOp",EDGE,"E93.filletArc"),sQuery(id+"F0.wireOp",EDGE,"E94.filletArc"),sQuery(id+"F0.wireOp",EDGE,"E95"),sQuery(id+"F0.wireOp",EDGE,"E96.filletArc"),sQuery(id+"F0.wireOp",EDGE,"E97.filletArc"),sQuery(id+"F0.wireOp",EDGE,"E98.filletArc"),sQuery(id+"F0.wireOp",EDGE,"E99.filletArc"),sQuery(id+"F0.wireOp",EDGE,"E100.filletArc"),sQuery(id+"F0.wireOp",EDGE,"E101.filletArc"),sQuery(id+"F0.wireOp",EDGE,"E102.filletArc"),sQuery(id+"F0.wireOp",EDGE,"E103.filletArc"),sQuery(id+"F0.wireOp",EDGE,"E104.filletArc"),sQuery(id+"F0.wireOp",EDGE,"E105.filletArc"),sQuery(id+"F0.wireOp",EDGE,"E106.filletArc"),sQuery(id+"F0.wireOp",EDGE,"E107.filletArc"),sQuery(id+"F0.wireOp",EDGE,"E108.filletArc"),sQuery(id+"F0.wireOp",EDGE,"E109.filletArc"),sQuery(id+"F0.wireOp",EDGE,"E110.filletArc"),sQuery(id+"F0.wireOp",EDGE,"E111.filletArc"),sQuery(id+"F0.wireOp",EDGE,"E112.filletArc"),sQuery(id+"F0.wireOp",EDGE,"E113.filletArc"),sQuery(id+"F0.wireOp",EDGE,"E118.filletArc"),sQuery(id+"F0.wireOp",EDGE,"E121.filletArc"),sQuery(id+"F0.wireOp",EDGE,"E122.filletArc"),sQuery(id+"F0.wireOp",EDGE,"E125.filletArc"),sQuery(id+"F0.wireOp",EDGE,"E126.filletArc"),sQuery(id+"F0.wireOp",EDGE,"E129.filletArc"),sQuery(id+"F0.wireOp",EDGE,"E130.filletArc"),sQuery(id+"F0.wireOp",EDGE,"E133.filletArc"),sQuery(id+"F0.wireOp",EDGE,"E134.filletArc"),sQuery(id+"F0.wireOp",EDGE,"E144.filletArc"),sQuery(id+"F0.wireOp",EDGE,"E145.filletArc")])],"isStart":false});
            cPlane(context, id + "F12", {"entities" : qUnion([Q0]), "cplaneType" : CPlaneType.OFFSET, "offset" : 20 * mm, "oppositeDirection" : true, "width" : 150 * mm, "height" : 150 * mm});
        }
        {
            var Q0;
            Q0=qCreatedBy(id+"F12.planeOp",FACE);
            var sketch = newSketch(context, id + "F13", { "sketchPlane" : qUnion([Q0])});
            skCircle(sketch, "E163.0", {"center": v(0, 25.5) * mm, "radius": 10.96 * mm});
            skSolve(sketch);
        }
        {
            var Q0;
            Q0=makeQuery(id+"F13.imprint","IMPRINT",FACE,{"disambiguationData":[TD([[makeQuery(id+"F13.imprint","IMPRINT",EDGE,{"derivedFrom":sQuery(id+"F13.wireOp",EDGE,"E163.0")}),1.0]])]});
            extrude(context, id + "F14", {"entities" : qUnion([Q0]), "operationType" : NewBodyOperationType.REMOVE, "oppositeDirection" : true, "depth" : 20 * mm, "offsetDistance" : 25 * mm});
        }
        {
            var Q0;
            Q0=makeQuery(id+"F14.boolean.opBoolean","INTERSECT",EDGE,{"derivedFrom":[makeQuery(id+"F1.opExtrude","SWEPT_FACE",FACE,{"disambiguationData":[OSD([sQuery(id+"F0.wireOp",EDGE,"E48")])]}),makeQuery(id+"F14.opExtrude","CAP_FACE",FACE,{"disambiguationData":[OSD([sQuery(id+"F13.wireOp",EDGE,"E163.0")])],"isStart":true})]});
            var Q1;
            Q1=makeQuery(id+"F14.boolean.opBoolean","INTERSECT",EDGE,{"derivedFrom":[makeQuery(id+"F1.opExtrude","SWEPT_FACE",FACE,{"disambiguationData":[OSD([sQuery(id+"F0.wireOp",EDGE,"E48")])]}),makeQuery(id+"F14.opExtrude","CAP_FACE",FACE,{"disambiguationData":[OSD([sQuery(id+"F13.wireOp",EDGE,"E163.0")])],"isStart":false})]});
            var Q2;
            Q2=makeQuery(id+"F1.opExtrude","CAP_EDGE",EDGE,{"disambiguationData":[OSD([sQuery(id+"F0.wireOp",EDGE,"E48")])],"isStart":true});
            var Q3;
            Q3=makeQuery(id+"F1.opExtrude","CAP_EDGE",EDGE,{"disambiguationData":[OSD([sQuery(id+"F0.wireOp",EDGE,"E48")])],"isStart":false});
            var Q4;
            Q4=makeQuery(id+"F14.boolean.opBoolean","COPY",EDGE,{"derivedFrom":makeQuery(id+"F14.opExtrude","CAP_EDGE",EDGE,{"disambiguationData":[OSD([sQuery(id+"F13.wireOp",EDGE,"E163.0")])],"isStart":false})});
            var Q5;
            Q5=makeQuery(id+"F14.boolean.opBoolean","COPY",EDGE,{"derivedFrom":makeQuery(id+"F14.opExtrude","CAP_EDGE",EDGE,{"disambiguationData":[OSD([sQuery(id+"F13.wireOp",EDGE,"E163.0")])],"isStart":true})});
            var Q6;
            Q6=makeQuery(id+"F1.opExtrude","CAP_EDGE",EDGE,{"disambiguationData":[OSD([sQuery(id+"F0.wireOp",EDGE,"E51")])],"isStart":true});
            var Q7;
            Q7=makeQuery(id+"F1.opExtrude","CAP_EDGE",EDGE,{"disambiguationData":[OSD([sQuery(id+"F0.wireOp",EDGE,"E51")])],"isStart":false});
            fillet(context, id + "F15", {"entities" : qUnion([Q0, Q1, Q2, Q3, Q4, Q5, Q6, Q7]), "radius" : 3 * mm, "tangentPropagation" : true, "allowEdgeOverflow" : false});
        }
        {
            var Q0;
            Q0=makeQuery(id+"F14.boolean.opBoolean","INTERSECT",EDGE,{"derivedFrom":[makeQuery(id+"F1.opExtrude","SWEPT_FACE",FACE,{"disambiguationData":[OSD([sQuery(id+"F0.wireOp",EDGE,"E52")])]}),makeQuery(id+"F14.opExtrude","SWEPT_FACE",FACE,{"disambiguationData":[OSD([sQuery(id+"F13.wireOp",EDGE,"E163.0")])]})]});
            var Q1;
            Q1=makeQuery(id+"F14.boolean.opBoolean","INTERSECT",EDGE,{"derivedFrom":[makeQuery(id+"F1.opExtrude","SWEPT_FACE",FACE,{"disambiguationData":[OSD([sQuery(id+"F0.wireOp",EDGE,"E53")])]}),makeQuery(id+"F14.opExtrude","SWEPT_FACE",FACE,{"disambiguationData":[OSD([sQuery(id+"F13.wireOp",EDGE,"E163.0")])]})]});
            fillet(context, id + "F16", {"entities" : qUnion([Q0, Q1]), "radius" : 1 * mm, "tangentPropagation" : true, "allowEdgeOverflow" : false});
        }
        {
            var Q0;
            Q0=makeQuery(id+"F14.boolean.opBoolean","INTERSECT",EDGE,{"derivedFrom":[makeQuery(id+"F1.opExtrude","SWEPT_FACE",FACE,{"disambiguationData":[OSD([sQuery(id+"F0.wireOp",EDGE,"E51")])]}),makeQuery(id+"F14.opExtrude","CAP_FACE",FACE,{"disambiguationData":[OSD([sQuery(id+"F13.wireOp",EDGE,"E163.0")])],"isStart":false})]});
            var Q1;
            Q1=makeQuery(id+"F14.boolean.opBoolean","INTERSECT",EDGE,{"derivedFrom":[makeQuery(id+"F1.opExtrude","SWEPT_FACE",FACE,{"disambiguationData":[OSD([sQuery(id+"F0.wireOp",EDGE,"E51")])]}),makeQuery(id+"F14.opExtrude","CAP_FACE",FACE,{"disambiguationData":[OSD([sQuery(id+"F13.wireOp",EDGE,"E163.0")])],"isStart":true})]});
            fillet(context, id + "F17", {"entities" : qUnion([Q0, Q1]), "radius" : 1 * mm, "tangentPropagation" : true, "allowEdgeOverflow" : false});
        }
    });
